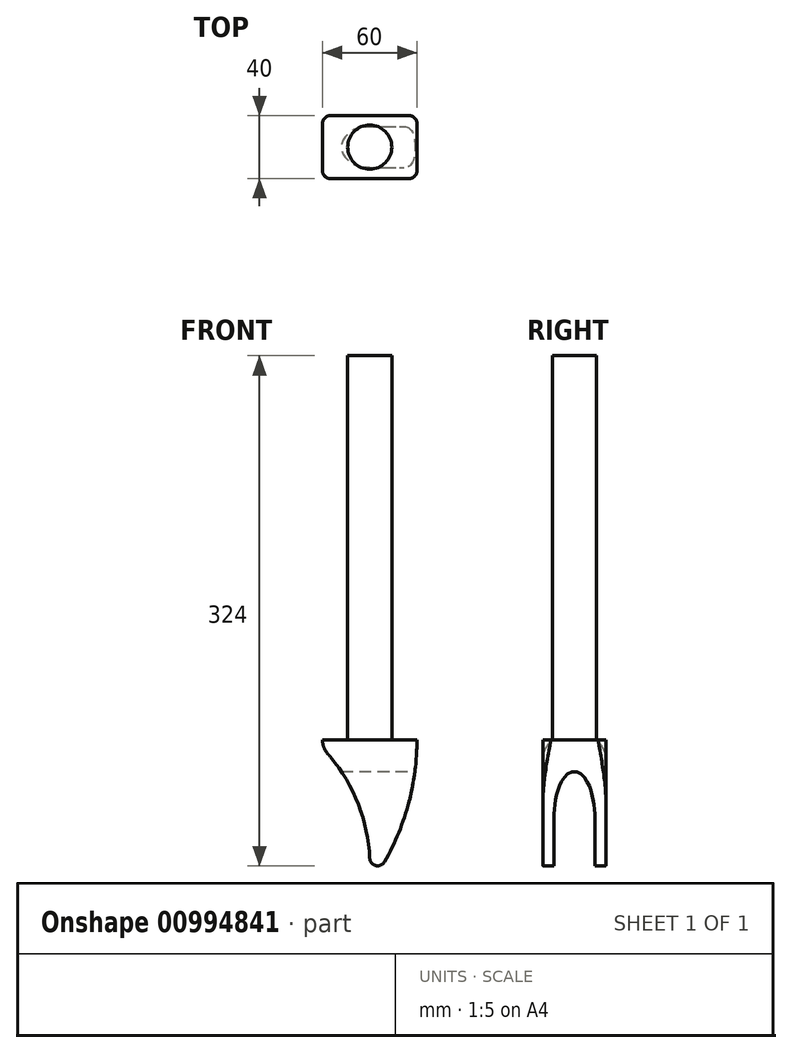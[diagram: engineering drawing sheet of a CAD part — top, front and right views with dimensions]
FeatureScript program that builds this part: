
annotation { "Feature Type Name" : "Feature", "Feature Type Description" : "" }
export const myFeature = defineFeature(function(context is Context, id is Id, definition is map)
    precondition{}
    {
        {
            var Q0;
            Q0=qCreatedBy(makeId("Top.planeOp"),FACE);
            var sketch = newSketch(context, id + "F0", { "sketchPlane" : qUnion([Q0])});
            skCircle(sketch, "E0", {"center": v(0, 0) * mm, "radius": 14 * mm});
            skSolve(sketch);
        }
        {
            var Q0;
            Q0=makeQuery(id+"F0.imprint","IMPRINT",FACE,{"disambiguationData":[TD([[makeQuery(id+"F0.imprint","IMPRINT",EDGE,{"derivedFrom":sQuery(id+"F0.wireOp",EDGE,"E0")}),1.0]])]});
            extrude(context, id + "F1", {"entities" : qUnion([Q0]), "depth" : 244 * mm, "offsetDistance" : 25 * mm});
        }
        {
            var Q0;
            Q0=qCreatedBy(makeId("Top.planeOp"),FACE);
            var sketch = newSketch(context, id + "F2", { "sketchPlane" : qUnion([Q0])});
            skLineSegment(sketch, "E1.bottom", {"start": v(30, 20) * mm, "end": v(-30, 20) * mm});
            skLineSegment(sketch, "E1.top", {"start": v(30, -20) * mm, "end": v(-30, -20) * mm});
            skLineSegment(sketch, "E1.left", {"start": v(30, 20) * mm, "end": v(30, -20) * mm});
            skLineSegment(sketch, "E1.right", {"start": v(-30, 20) * mm, "end": v(-30, -20) * mm});
            skPoint(sketch, "E1.middle", {"position": v(0, 0) * mm});
            skSolve(sketch);
        }
        {
            var Q0;
            Q0=makeQuery(id+"F2.imprint","IMPRINT",FACE,{"disambiguationData":[TD([[makeQuery(id+"F2.imprint","IMPRINT",EDGE,{"derivedFrom":sQuery(id+"F2.wireOp",EDGE,"E1.bottom")}),1.0]])]});
            extrude(context, id + "F3", {"entities" : qUnion([Q0]), "operationType" : NewBodyOperationType.ADD, "oppositeDirection" : true, "depth" : 80 * mm, "offsetDistance" : 25 * mm});
        }
        {
            var Q0;
            Q0=makeQuery(id+"F3.opExtrude","SWEPT_EDGE",EDGE,{"disambiguationData":[OSD([sQuery(id+"F2.wireOp",EDGE,"E1.top"),sQuery(id+"F2.wireOp",EDGE,"E1.left")])]});
            var Q1;
            Q1=makeQuery(id+"F3.opExtrude","SWEPT_EDGE",EDGE,{"disambiguationData":[OSD([sQuery(id+"F2.wireOp",EDGE,"E1.top"),sQuery(id+"F2.wireOp",EDGE,"E1.right")])]});
            var Q2;
            Q2=makeQuery(id+"F3.opExtrude","SWEPT_EDGE",EDGE,{"disambiguationData":[OSD([sQuery(id+"F2.wireOp",EDGE,"E1.bottom"),sQuery(id+"F2.wireOp",EDGE,"E1.left")])]});
            var Q3;
            Q3=makeQuery(id+"F3.opExtrude","SWEPT_EDGE",EDGE,{"disambiguationData":[OSD([sQuery(id+"F2.wireOp",EDGE,"E1.bottom"),sQuery(id+"F2.wireOp",EDGE,"E1.right")])]});
            fillet(context, id + "F4", {"entities" : qUnion([Q0, Q1, Q2, Q3]), "radius" : 5 * mm, "tangentPropagation" : true, "allowEdgeOverflow" : false});
        }
        {
            var Q0;
            Q0=qCreatedBy(makeId("Front.planeOp"),FACE);
            var sketch = newSketch(context, id + "F5", { "sketchPlane" : qUnion([Q0])});
            skLineSegment(sketch, "E2.0", {"start": v(-30, -90) * mm, "end": v(-30, 0) * mm});
            skLineSegment(sketch, "E3.0", {"start": v(30, 0) * mm, "end": v(30, -90) * mm});
            skArc(sketch, "E4", {"start": v(-30, 0) * mm, "mid": v(-29.15, -4.7) * mm, "end": v(-26.7, -8.79) * mm});
            skArc(sketch, "E5", {"start": v(0, -75.22) * mm, "mid": v(-7.68, -39.73) * mm, "end": v(-26.7, -8.79) * mm});
            skArc(sketch, "E6", {"start": v(9.34, -77.49) * mm, "mid": v(24.75, -40.1) * mm, "end": v(30, 0) * mm});
            skArc(sketch, "E7", {"start": v(0, -75.22) * mm, "mid": v(3.82, -79.86) * mm, "end": v(9.34, -77.49) * mm});
            skLineSegment(sketch, "E8.0", {"start": v(30, -90) * mm, "end": v(-30, -90) * mm});
            skSolve(sketch);
        }
        {
            var Q0;
            Q0=qSketchRegion(id+"F5",true);
            extrude(context, id + "F6", {"entities" : qUnion([Q0]), "operationType" : NewBodyOperationType.REMOVE, "endBound" : BoundingType.SYMMETRIC, "oppositeDirection" : true, "depth" : 80 * mm, "offsetDistance" : 25 * mm});
        }
        {
            var Q0;
            Q0=qCreatedBy(makeId("Right.planeOp"),FACE);
            var sketch = newSketch(context, id + "F7", { "sketchPlane" : qUnion([Q0])});
            skEllipticalArc(sketch, "E9", {});
            skLineSegment(sketch, "E10", {"start": v(13, -50) * mm, "end": v(13, -80) * mm});
            skLineSegment(sketch, "E11", {"start": v(-13, -50) * mm, "end": v(-13, -80) * mm});
            skLineSegment(sketch, "E12", {"start": v(-13, -80) * mm, "end": v(13, -80) * mm});
            skPoint(sketch, "E13", {"position": v(0, -20) * mm});
            const initialGuessF7  = {"E9": [0, -0.05, 0, -1, 0.03, 0.013, 1.5707963267948968, 4.71238898038469]};
            skSetInitialGuess(sketch, initialGuessF7);
            skSolve(sketch);
        }
        {
            var Q0;
            Q0=qSketchRegion(id+"F7",true);
            extrude(context, id + "F8", {"entities" : qUnion([Q0]), "operationType" : NewBodyOperationType.REMOVE, "endBound" : BoundingType.SYMMETRIC, "oppositeDirection" : true, "depth" : 70 * mm, "offsetDistance" : 25 * mm});
        }
    });
